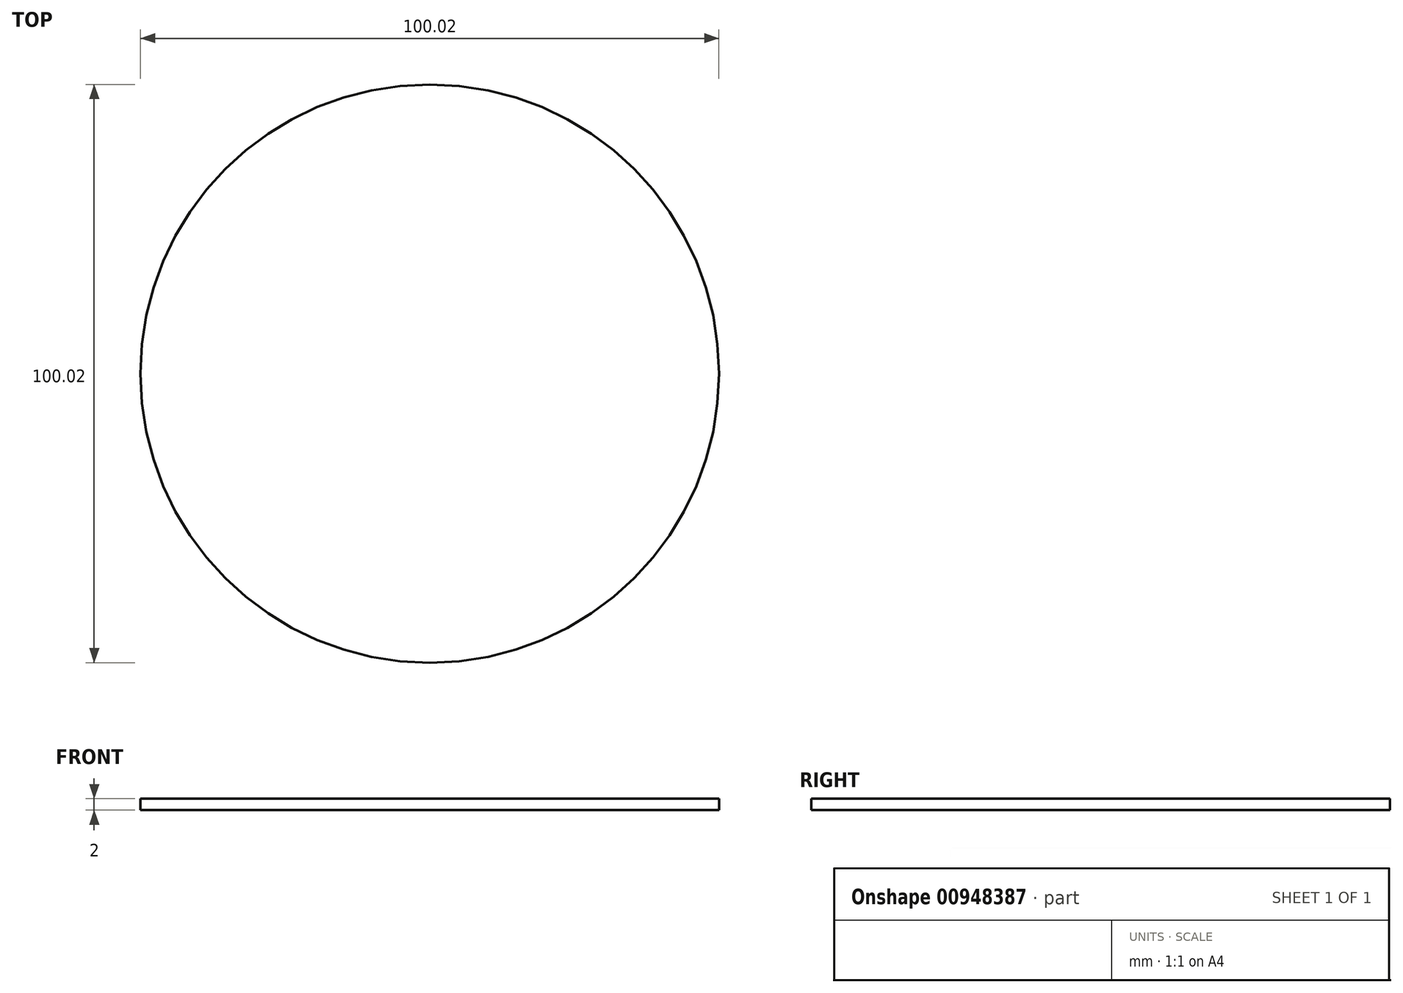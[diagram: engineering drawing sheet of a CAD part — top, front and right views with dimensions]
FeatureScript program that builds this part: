
annotation { "Feature Type Name" : "Feature", "Feature Type Description" : "" }
export const myFeature = defineFeature(function(context is Context, id is Id, definition is map)
    precondition{}
    {
        {
            var Q0;
            Q0=qCreatedBy(makeId("Top.planeOp"),FACE);
            var sketch = newSketch(context, id + "F0", { "sketchPlane" : qUnion([Q0])});
            skCircle(sketch, "E0", {"center": v(0, 0) * mm, "radius": 50.01 * mm});
            skSolve(sketch);
        }
        {
            var Q0;
            Q0=makeQuery(id+"F0.imprint","IMPRINT",FACE,{"disambiguationData":[TD([[makeQuery(id+"F0.imprint","IMPRINT",EDGE,{"derivedFrom":sQuery(id+"F0.wireOp",EDGE,"E0")}),1.0]])]});
            extrude(context, id + "F1", {"entities" : qUnion([Q0]), "depth" : 2 * mm, "offsetDistance" : 25 * mm});
        }
    });
